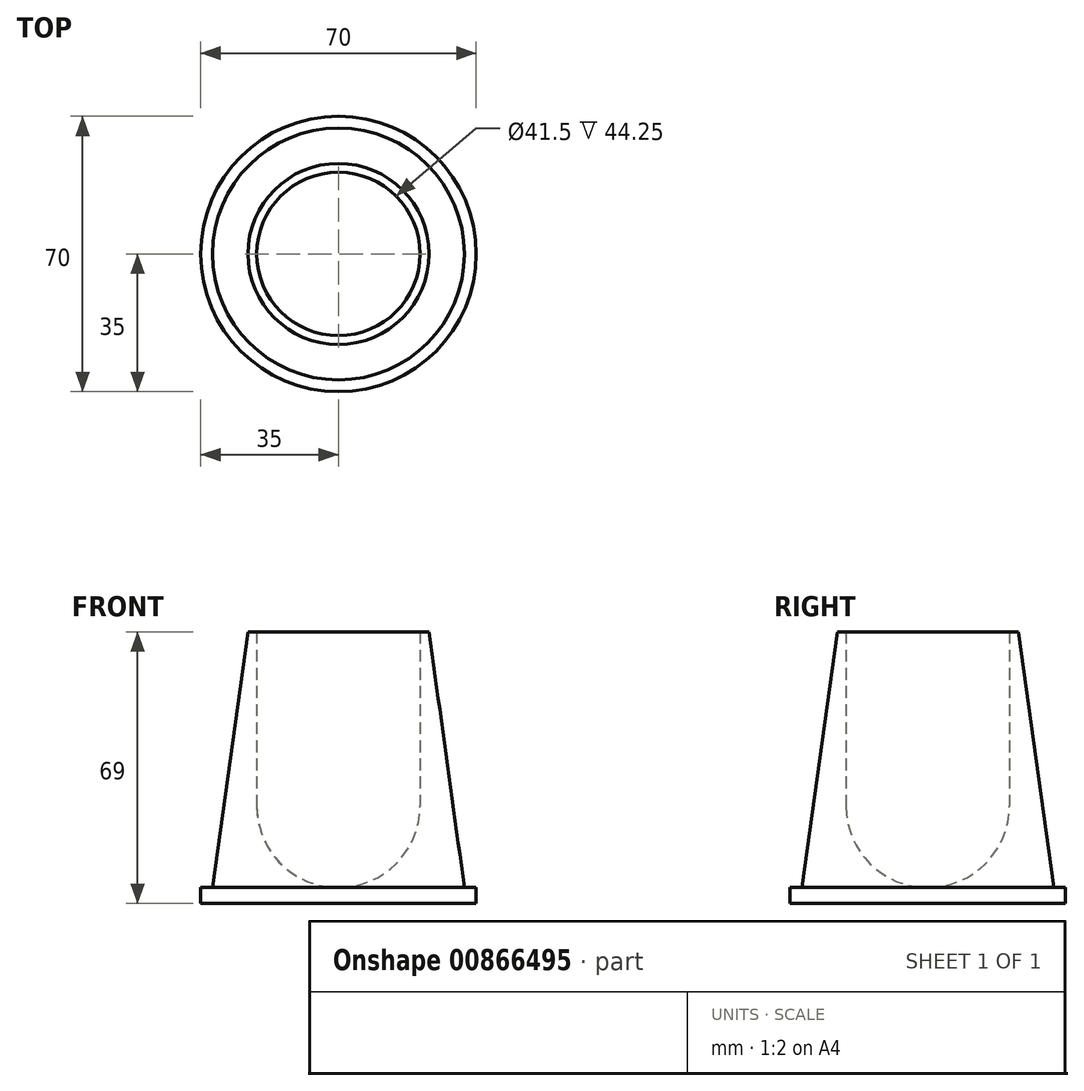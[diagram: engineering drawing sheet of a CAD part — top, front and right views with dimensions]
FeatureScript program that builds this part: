
annotation { "Feature Type Name" : "Feature", "Feature Type Description" : "" }
export const myFeature = defineFeature(function(context is Context, id is Id, definition is map)
    precondition{}
    {
        {
            var Q0;
            Q0=qCreatedBy(makeId("Top.planeOp"),FACE);
            var sketch = newSketch(context, id + "F0", { "sketchPlane" : qUnion([Q0])});
            skCircle(sketch, "E0", {"center": v(0, 0) * mm, "radius": 35 * mm});
            skSolve(sketch);
        }
        {
            var Q0;
            Q0=makeQuery(id+"F0.imprint","IMPRINT",FACE,{"disambiguationData":[TD([[makeQuery(id+"F0.imprint","IMPRINT",EDGE,{"derivedFrom":sQuery(id+"F0.wireOp",EDGE,"E0")}),1.0]])]});
            extrude(context, id + "F1", {"entities" : qUnion([Q0]), "depth" : 4 * mm, "offsetDistance" : 25 * mm});
        }
        {
            var Q0;
            Q0=makeQuery(id+"F1.opExtrude","CAP_FACE",FACE,{"disambiguationData":[OSD([sQuery(id+"F0.wireOp",EDGE,"E0")])],"isStart":false});
            cPlane(context, id + "F2", {"entities" : qUnion([Q0]), "cplaneType" : CPlaneType.OFFSET, "offset" : 65 * mm, "width" : 150 * mm, "height" : 150 * mm});
        }
        {
            var Q0;
            Q0=qCreatedBy(id+"F2.planeOp",FACE);
            var sketch = newSketch(context, id + "F3", { "sketchPlane" : qUnion([Q0])});
            skCircle(sketch, "E1", {"center": v(0, 0) * mm, "radius": 23 * mm});
            skSolve(sketch);
        }
        {
            var Q0;
            Q0=makeQuery(id+"F1.opExtrude","CAP_FACE",FACE,{"disambiguationData":[OSD([sQuery(id+"F0.wireOp",EDGE,"E0")])],"isStart":false});
            var sketch = newSketch(context, id + "F4", { "sketchPlane" : qUnion([Q0])});
            skCircle(sketch, "E2.0", {"center": v(0, 0) * mm, "radius": 35 * mm, "construction": true});
            skCircle(sketch, "E3.0", {"center": v(0, 0) * mm, "radius": 32 * mm});
            skSolve(sketch);
        }
        {
            var Q1;
            Q1=makeQuery(id+"F4.imprint","IMPRINT",FACE,{"disambiguationData":[TD([[makeQuery(id+"F4.imprint","IMPRINT",EDGE,{"derivedFrom":sQuery(id+"F4.wireOp",EDGE,"E3.0")}),1.0]])]});
            var Q2;
            Q2=makeQuery(id+"F3.imprint","IMPRINT",FACE,{"disambiguationData":[TD([[makeQuery(id+"F3.imprint","IMPRINT",EDGE,{"derivedFrom":sQuery(id+"F3.wireOp",EDGE,"E1")}),1.0]])]});
            loft(context, id + "F5", {"operationType" : NewBodyOperationType.ADD, "sheetProfilesArray" : [{ "sheetProfileEntities" : qUnion([Q1]) }, { "sheetProfileEntities" : qUnion([Q2]) }]});
        }
        {
            var Q0;
            Q0=qCreatedBy(makeId("Front.planeOp"),FACE);
            var sketch = newSketch(context, id + "F6", { "sketchPlane" : qUnion([Q0])});
            skLineSegment(sketch, "E4.0", {"start": v(-23, 69) * mm, "end": v(23, 69) * mm, "construction": true});
            skLineSegment(sketch, "E5", {"start": v(0, 69) * mm, "end": v(0, 4) * mm});
            skLineSegment(sketch, "E6.0", {"start": v(-20.75, 69) * mm, "end": v(-20.75, 24.75) * mm});
            skArc(sketch, "E7", {"start": v(-20.75, 24.75) * mm, "mid": v(-14.67, 10.08) * mm, "end": v(0, 4) * mm});
            skLineSegment(sketch, "E8", {"start": v(-20.75, 69) * mm, "end": v(0, 69) * mm});
            skSolve(sketch);
        }
        {
            var Q0;
            Q0 = qSketchRegion(id + "F6", true);
            var Q1;
            Q1=sQuery(id+"F6.wireOp",EDGE,"E5");
            revolve(context, id + "F7", {"operationType" : NewBodyOperationType.REMOVE, "surfaceOperationType" : NewSurfaceOperationType.NEW, "entities" : qUnion([Q0]), "axis" : qUnion([Q1]), "revolveType" : RevolveType.FULL, "oppositeDirection" : true});
        }
    });
